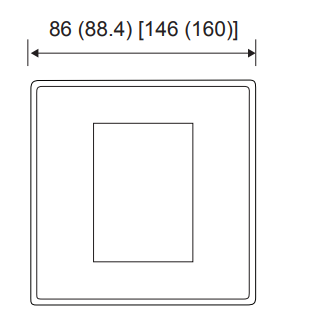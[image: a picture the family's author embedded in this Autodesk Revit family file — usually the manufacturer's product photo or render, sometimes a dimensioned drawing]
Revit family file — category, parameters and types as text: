
# Revit family: Fascia Panel_232S
name_source: partatom
category: Electrical Fixtures
revit_build: Autodesk Revit 2018 (Build: 20170223_1515(x64)
units: mm (PartAtom-declared; Revit-internal decimal feet)

## family parameters
Always vertical = Yes
Cut with Voids When Loaded = No
Maintain Annotation Orientation = No
Part Type = Normal
Room Calculation Point = No
Round Connector Dimension = Use Diameter
Shared = No
Work Plane-Based = Yes

## types (1)
- SG stainless steel plate with grid
    Default Elevation = 0 mm  [stored 0 ft]
    Manufacturer = Helvar
    Model = 232 S
    Single chassis dimension = 86 mm × 86 mm × 5.9 mm
    Single frame dimension = 86 mm × 86 mm × 4.5 mm
(Plastic: 88.4 mm × 88.4 mm × 4.5
mm)
    Single frame kit -net weight = 100 g

note: [stored X ft] marks values corroborated as IEEE doubles in the binary element streams (Revit-internal decimal feet)

## geometry (parser evidence)
native form markers: Sweep x4
no freeform markers — native parametric forms only
